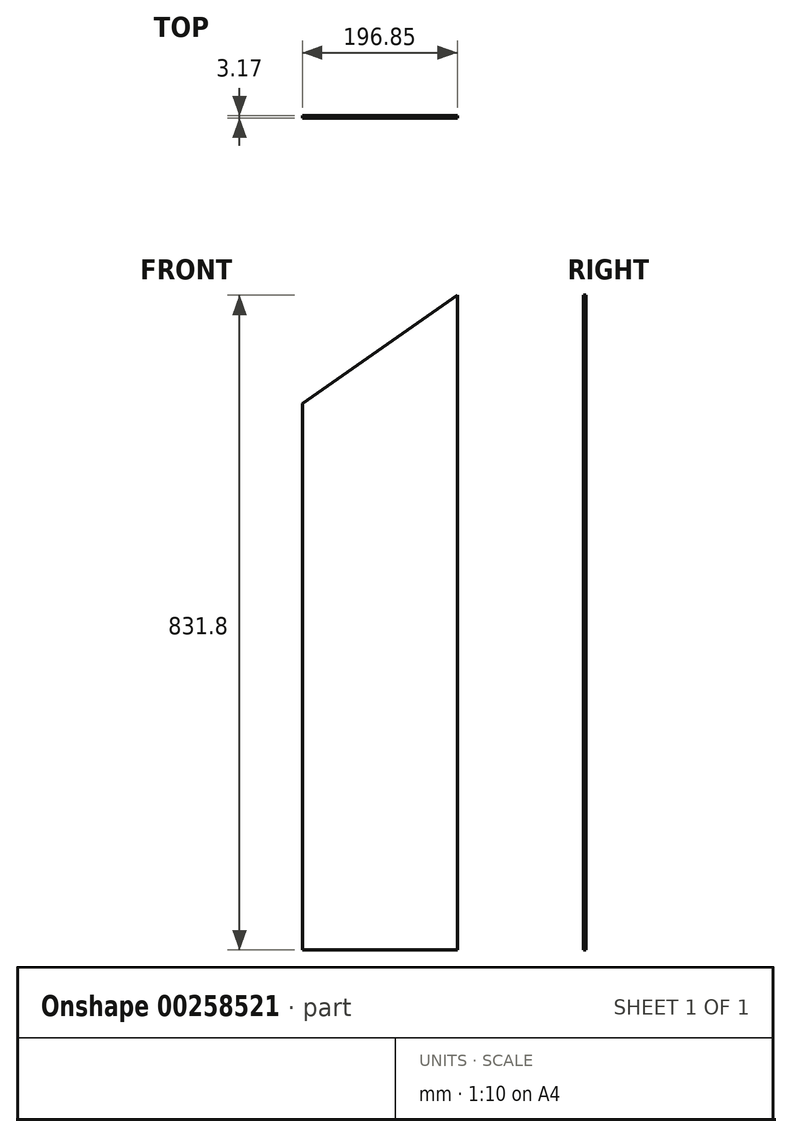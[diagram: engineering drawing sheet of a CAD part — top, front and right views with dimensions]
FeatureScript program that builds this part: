
annotation { "Feature Type Name" : "Feature", "Feature Type Description" : "" }
export const myFeature = defineFeature(function(context is Context, id is Id, definition is map)
    precondition{}
    {
        {
            var Q0;
            Q0=qCreatedBy(makeId("Front.planeOp"),FACE);
            var sketch = newSketch(context, id + "F0", { "sketchPlane" : qUnion([Q0])});
            skLineSegment(sketch, "E0.top", {"start": v(98.43, -415.9) * mm, "end": v(-98.43, -415.9) * mm});
            skLineSegment(sketch, "E0.left", {"start": v(98.43, 415.9) * mm, "end": v(98.43, -415.9) * mm});
            skLineSegment(sketch, "E0.right", {"start": v(-98.43, 278.07) * mm, "end": v(-98.43, -415.9) * mm});
            skPoint(sketch, "E0.middle", {"position": v(0, 0) * mm});
            skLineSegment(sketch, "E1", {"start": v(98.43, 415.9) * mm, "end": v(-98.43, 278.07) * mm});
            skPoint(sketch, "E2.orphan", {"position": v(-98.42, 415.9) * mm});
            skSolve(sketch);
        }
        {
            var Q0;
            Q0 = qSketchRegion(id + "F0", true);
            extrude(context, id + "F1", {"entities" : qUnion([Q0]), "depth" : 3.17 * mm});
        }
    });
